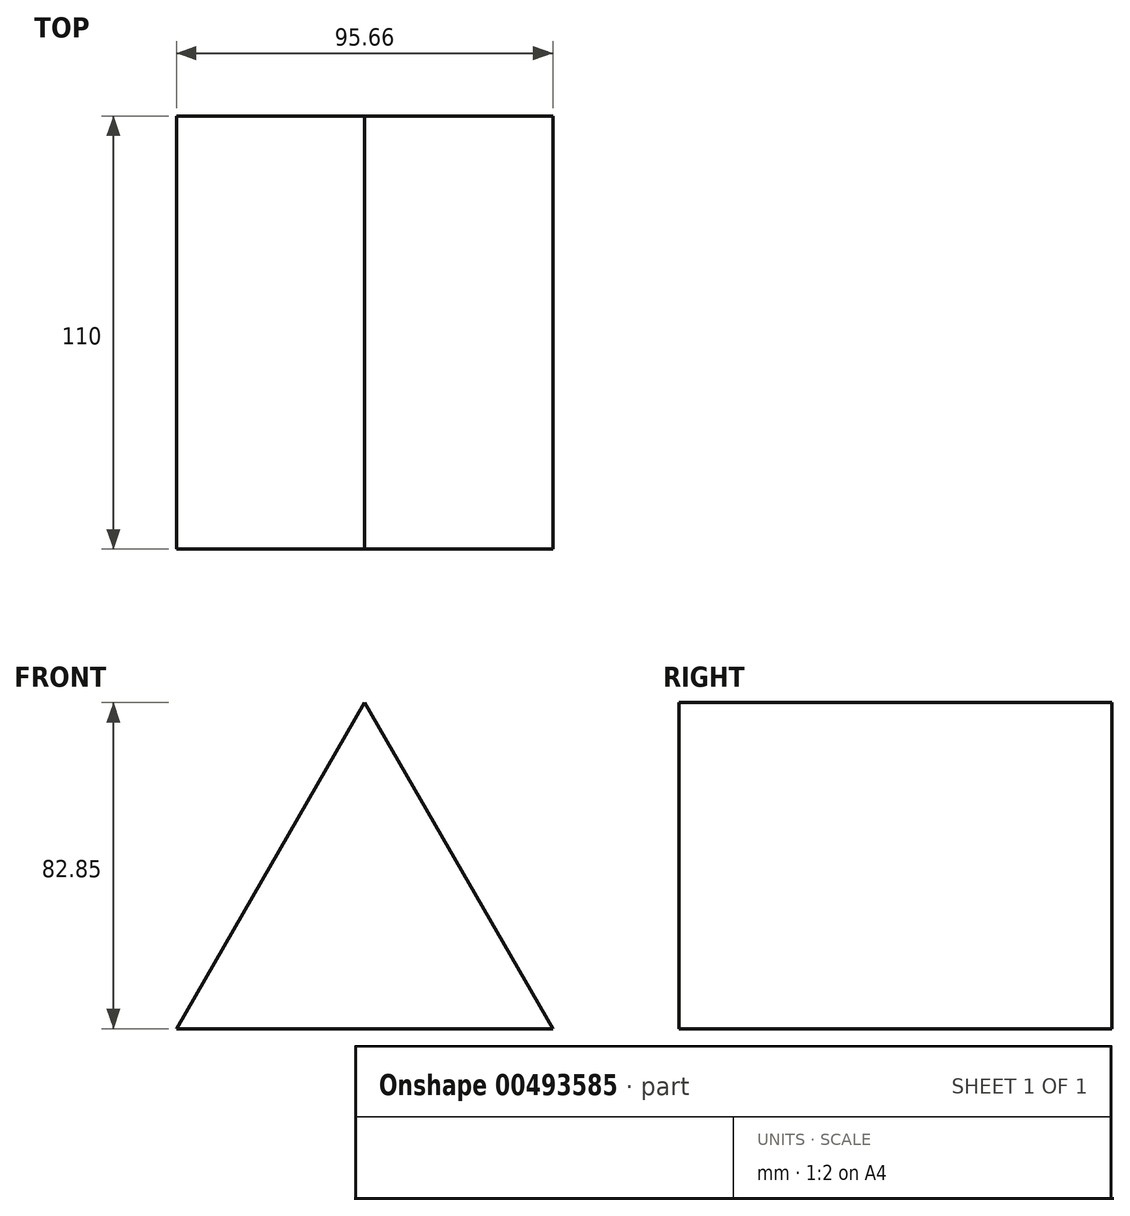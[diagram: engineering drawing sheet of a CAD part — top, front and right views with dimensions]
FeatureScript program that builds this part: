
annotation { "Feature Type Name" : "Feature", "Feature Type Description" : "" }
export const myFeature = defineFeature(function(context is Context, id is Id, definition is map)
    precondition{}
    {
        {
            var Q0;
            Q0=qCreatedBy(makeId("Front.planeOp"),FACE);
            var sketch = newSketch(context, id + "F0", { "sketchPlane" : qUnion([Q0])});
            skCircle(sketch, "E0.cCircle", {"center": v(0, 0) * mm, "radius": 55.23 * mm, "construction": true});
            skLineSegment(sketch, "E0.0", {"start": v(-47.83, -27.62) * mm, "end": v(0, 55.23) * mm});
            skLineSegment(sketch, "E0.1", {"start": v(0, 55.23) * mm, "end": v(47.83, -27.62) * mm});
            skLineSegment(sketch, "E0.2", {"start": v(47.83, -27.62) * mm, "end": v(-47.83, -27.62) * mm});
            skSolve(sketch);
        }
        {
            var Q0;
            Q0=makeQuery(id+"F0.imprint","IMPRINT",FACE,{"disambiguationData":[TD([[makeQuery(id+"F0.imprint","IMPRINT",EDGE,{"derivedFrom":sQuery(id+"F0.wireOp",EDGE,"E0.0")}),-1.0]])]});
            extrude(context, id + "F1", {"entities" : qUnion([Q0]), "endBound" : BoundingType.SYMMETRIC, "depth" : 110 * mm});
        }
    });
